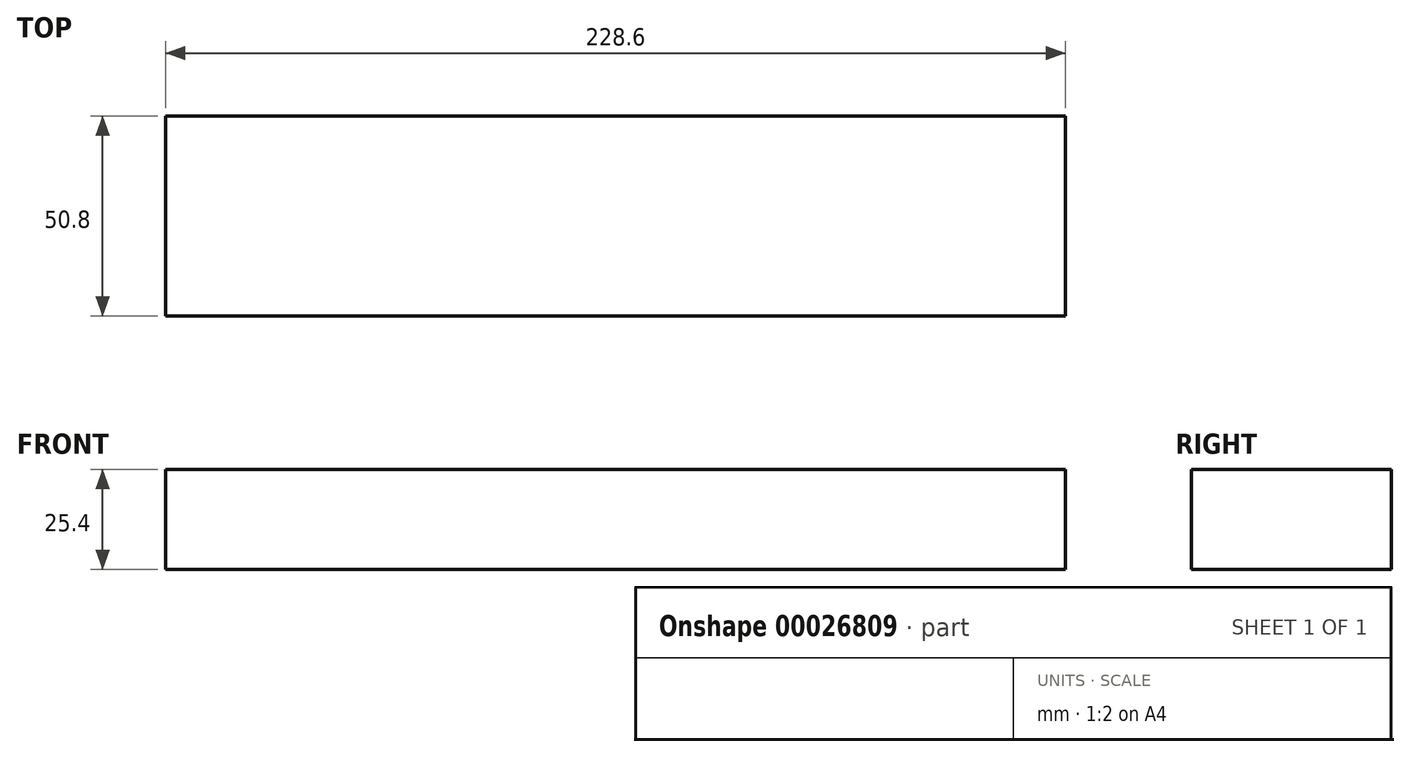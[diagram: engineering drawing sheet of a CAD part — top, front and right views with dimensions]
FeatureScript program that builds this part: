
annotation { "Feature Type Name" : "Feature", "Feature Type Description" : "" }
export const myFeature = defineFeature(function(context is Context, id is Id, definition is map)
    precondition{}
    {
        {
            var Q0;
            Q0=qCreatedBy(makeId("Top.planeOp"),FACE);
            var sketch = newSketch(context, id + "F0", { "sketchPlane" : qUnion([Q0])});
            skLineSegment(sketch, "E0.bottom", {"start": v(-79.98, -22.87) * mm, "end": v(148.62, -22.87) * mm});
            skLineSegment(sketch, "E0.top", {"start": v(-79.98, 27.93) * mm, "end": v(148.62, 27.93) * mm});
            skLineSegment(sketch, "E0.left", {"start": v(-79.98, -22.87) * mm, "end": v(-79.98, 27.93) * mm});
            skLineSegment(sketch, "E0.right", {"start": v(148.62, -22.87) * mm, "end": v(148.62, 27.93) * mm});
            skSolve(sketch);
        }
        {
            var Q0;
            Q0=makeQuery(id+"F0.imprint","IMPRINT",FACE,{"disambiguationData":[TD([[makeQuery(id+"F0.imprint","IMPRINT",EDGE,{"derivedFrom":sQuery(id+"F0.wireOp",EDGE,"E0.bottom")}),1.0]])]});
            extrude(context, id + "F1", {"entities" : qUnion([Q0]), "depth" : 25.4 * mm});
        }
    });
